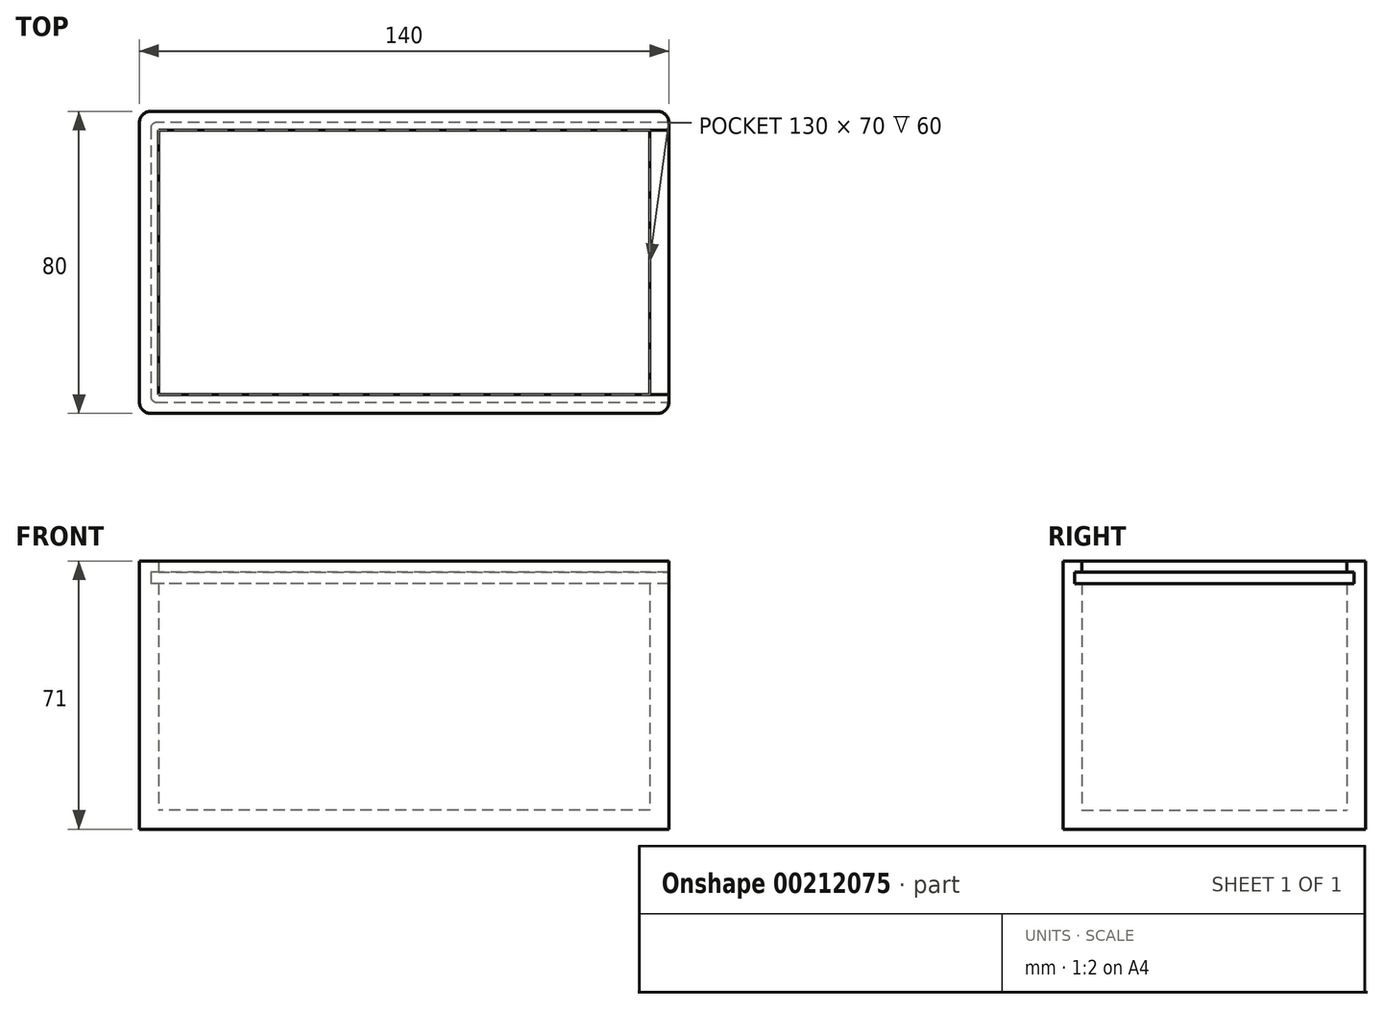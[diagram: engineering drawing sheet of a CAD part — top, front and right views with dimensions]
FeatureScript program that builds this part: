
annotation { "Feature Type Name" : "Feature", "Feature Type Description" : "" }
export const myFeature = defineFeature(function(context is Context, id is Id, definition is map)
    precondition{}
    {
        {
            var Q0;
            Q0=qCreatedBy(makeId("Top.planeOp"),FACE);
            var sketch = newSketch(context, id + "F0", { "sketchPlane" : qUnion([Q0])});
            skLineSegment(sketch, "E0.bottom", {"start": v(70, -40) * mm, "end": v(-70, -40) * mm});
            skLineSegment(sketch, "E0.top", {"start": v(70, 40) * mm, "end": v(-70, 40) * mm});
            skLineSegment(sketch, "E0.left", {"start": v(70, -40) * mm, "end": v(70, 40) * mm});
            skLineSegment(sketch, "E0.right", {"start": v(-70, -40) * mm, "end": v(-70, 40) * mm});
            skPoint(sketch, "E0.middle", {"position": v(0, 0) * mm});
            skLineSegment(sketch, "E1.bottom", {"start": v(65, -35) * mm, "end": v(-65, -35) * mm});
            skLineSegment(sketch, "E1.top", {"start": v(65, 35) * mm, "end": v(-65, 35) * mm});
            skLineSegment(sketch, "E1.left", {"start": v(65, -35) * mm, "end": v(65, 35) * mm});
            skLineSegment(sketch, "E1.right", {"start": v(-65, -35) * mm, "end": v(-65, 35) * mm});
            skSolve(sketch);
        }
        {
            var Q0;
            Q0=makeQuery(id+"F0.imprint","IMPRINT",FACE,{"disambiguationData":[TD([[makeQuery(id+"F0.imprint","IMPRINT",EDGE,{"derivedFrom":sQuery(id+"F0.wireOp",EDGE,"E0.bottom")}),-1.0]])]});
            extrude(context, id + "F1", {"entities" : qUnion([Q0]), "depth" : 70 * mm});
        }
        {
            var Q0;
            Q0=makeQuery(id+"F0.imprint","IMPRINT",FACE,{"disambiguationData":[TD([[makeQuery(id+"F0.imprint","IMPRINT",EDGE,{"derivedFrom":sQuery(id+"F0.wireOp",EDGE,"E1.bottom")}),-1.0]])]});
            extrude(context, id + "F2", {"entities" : qUnion([Q0]), "operationType" : NewBodyOperationType.ADD, "depth" : 5 * mm});
        }
        {
            var Q0;
            Q0=makeQuery(id+"F1.opExtrude","CAP_FACE",FACE,{"disambiguationData":[OSD([sQuery(id+"F0.wireOp",EDGE,"E0.bottom"),sQuery(id+"F0.wireOp",EDGE,"E0.top"),sQuery(id+"F0.wireOp",EDGE,"E0.left"),sQuery(id+"F0.wireOp",EDGE,"E0.right"),sQuery(id+"F0.wireOp",EDGE,"E1.bottom"),sQuery(id+"F0.wireOp",EDGE,"E1.top"),sQuery(id+"F0.wireOp",EDGE,"E1.left"),sQuery(id+"F0.wireOp",EDGE,"E1.right")])],"isStart":false});
            var sketch = newSketch(context, id + "F3", { "sketchPlane" : qUnion([Q0])});
            skLineSegment(sketch, "E2.bottom", {"start": v(65, 35) * mm, "end": v(70, 35) * mm});
            skLineSegment(sketch, "E2.top", {"start": v(65, -35) * mm, "end": v(70, -35) * mm});
            skLineSegment(sketch, "E2.left", {"start": v(65, 35) * mm, "end": v(65, -35) * mm});
            skLineSegment(sketch, "E2.right", {"start": v(70, 35) * mm, "end": v(70, -35) * mm});
            skSolve(sketch);
        }
        {
            var Q0;
            Q0=makeQuery(id+"F3.imprint","IMPRINT",FACE,{"disambiguationData":[TD([[makeQuery(id+"F3.imprint","IMPRINT",EDGE,{"derivedFrom":sQuery(id+"F3.wireOp",EDGE,"E2.bottom")}),-1.0]])]});
            extrude(context, id + "F4", {"entities" : qUnion([Q0]), "operationType" : NewBodyOperationType.REMOVE, "oppositeDirection" : true, "depth" : 5 * mm});
        }
        {
            var Q0;
            Q0=makeQuery(id+"F4.boolean.opBoolean","MERGE",FACE,{"derivedFrom":[makeQuery(id+"F1.opExtrude","SWEPT_FACE",FACE,{"disambiguationData":[OSD([sQuery(id+"F0.wireOp",EDGE,"E1.top")])]}),makeQuery(id+"F4.opExtrude","SWEPT_FACE",FACE,{"disambiguationData":[OSD([sQuery(id+"F3.wireOp",EDGE,"E2.bottom")])]})]});
            var sketch = newSketch(context, id + "F5", { "sketchPlane" : qUnion([Q0])});
            skLineSegment(sketch, "E3.bottom", {"start": v(70, 65) * mm, "end": v(-65, 65) * mm});
            skLineSegment(sketch, "E3.top", {"start": v(70, 68) * mm, "end": v(-65, 68) * mm});
            skLineSegment(sketch, "E3.left", {"start": v(70, 65) * mm, "end": v(70, 68) * mm});
            skLineSegment(sketch, "E3.right", {"start": v(-65, 65) * mm, "end": v(-65, 68) * mm});
            skSolve(sketch);
        }
        {
            var Q0;
            Q0=makeQuery(id+"F5.imprint","IMPRINT",FACE,{"disambiguationData":[TD([[makeQuery(id+"F5.imprint","IMPRINT",EDGE,{"derivedFrom":sQuery(id+"F5.wireOp",EDGE,"E3.bottom")}),-1.0]])]});
            extrude(context, id + "F6", {"entities" : qUnion([Q0]), "operationType" : NewBodyOperationType.REMOVE, "oppositeDirection" : true, "depth" : 2 * mm});
        }
        {
            var Q0;
            Q0=makeQuery(id+"F6.boolean.opBoolean","MERGE",FACE,{"derivedFrom":[makeQuery(id+"F1.opExtrude","SWEPT_FACE",FACE,{"disambiguationData":[OSD([sQuery(id+"F0.wireOp",EDGE,"E1.right")])]}),makeQuery(id+"F6.opExtrude","SWEPT_FACE",FACE,{"disambiguationData":[OSD([sQuery(id+"F5.wireOp",EDGE,"E3.right")])]})]});
            var sketch = newSketch(context, id + "F7", { "sketchPlane" : qUnion([Q0])});
            skLineSegment(sketch, "E4.bottom", {"start": v(37, 65) * mm, "end": v(-35, 65) * mm});
            skLineSegment(sketch, "E4.top", {"start": v(37, 68) * mm, "end": v(-35, 68) * mm});
            skLineSegment(sketch, "E4.left", {"start": v(37, 65) * mm, "end": v(37, 68) * mm});
            skLineSegment(sketch, "E4.right", {"start": v(-35, 65) * mm, "end": v(-35, 68) * mm});
            skSolve(sketch);
        }
        {
            var Q0;
            Q0=makeQuery(id+"F7.imprint","IMPRINT",FACE,{"disambiguationData":[TD([[makeQuery(id+"F7.imprint","IMPRINT",EDGE,{"derivedFrom":sQuery(id+"F7.wireOp",EDGE,"E4.bottom")}),-1.0]])]});
            extrude(context, id + "F8", {"entities" : qUnion([Q0]), "operationType" : NewBodyOperationType.REMOVE, "oppositeDirection" : true, "depth" : 2 * mm});
        }
        {
            var Q0;
            Q0=makeQuery(id+"F8.boolean.opBoolean","MERGE",FACE,{"derivedFrom":[makeQuery(id+"F4.boolean.opBoolean","MERGE",FACE,{"derivedFrom":[makeQuery(id+"F1.opExtrude","SWEPT_FACE",FACE,{"disambiguationData":[OSD([sQuery(id+"F0.wireOp",EDGE,"E1.bottom")])]}),makeQuery(id+"F4.opExtrude","SWEPT_FACE",FACE,{"disambiguationData":[OSD([sQuery(id+"F3.wireOp",EDGE,"E2.top")])]})]}),makeQuery(id+"F8.opExtrude","SWEPT_FACE",FACE,{"disambiguationData":[OSD([sQuery(id+"F7.wireOp",EDGE,"E4.right")])]})]});
            var sketch = newSketch(context, id + "F9", { "sketchPlane" : qUnion([Q0])});
            skLineSegment(sketch, "E5.bottom", {"start": v(67, 65) * mm, "end": v(-70, 65) * mm});
            skLineSegment(sketch, "E5.top", {"start": v(67, 68) * mm, "end": v(-70, 68) * mm});
            skLineSegment(sketch, "E5.left", {"start": v(67, 65) * mm, "end": v(67, 68) * mm});
            skLineSegment(sketch, "E5.right", {"start": v(-70, 65) * mm, "end": v(-70, 68) * mm});
            skSolve(sketch);
        }
        {
            var Q0;
            {var subQ17=sQuery(id+"F9.wireOp",EDGE,"E5.left");Q0=makeQuery(id+"F9.imprint","IMPRINT",FACE,{"disambiguationData":[TD([[makeQuery(id+"F9.imprint","IMPRINT",EDGE,{"derivedFrom":subQ17}),-1.0]])]});}
            extrude(context, id + "F10", {"entities" : qUnion([Q0]), "operationType" : NewBodyOperationType.REMOVE, "oppositeDirection" : true, "depth" : 2 * mm});
        }
        {
            var Q0;
            Q0=makeQuery(id+"F1.opExtrude","SWEPT_EDGE",EDGE,{"disambiguationData":[OSD([sQuery(id+"F0.wireOp",EDGE,"E0.bottom"),sQuery(id+"F0.wireOp",EDGE,"E0.right")])]});
            var Q1;
            Q1=makeQuery(id+"F1.opExtrude","SWEPT_EDGE",EDGE,{"disambiguationData":[OSD([sQuery(id+"F0.wireOp",EDGE,"E0.top"),sQuery(id+"F0.wireOp",EDGE,"E0.right")])]});
            var Q2;
            Q2=makeQuery(id+"F1.opExtrude","SWEPT_EDGE",EDGE,{"disambiguationData":[OSD([sQuery(id+"F0.wireOp",EDGE,"E0.top"),sQuery(id+"F0.wireOp",EDGE,"E0.left")])]});
            var Q3;
            Q3=makeQuery(id+"F1.opExtrude","SWEPT_EDGE",EDGE,{"disambiguationData":[OSD([sQuery(id+"F0.wireOp",EDGE,"E0.bottom"),sQuery(id+"F0.wireOp",EDGE,"E0.left")])]});
            fillet(context, id + "F11", {"entities" : qUnion([Q0, Q1, Q2, Q3]), "radius" : 3 * mm, "tangentPropagation" : true, "allowEdgeOverflow" : false});
        }
        {
            var Q0;
            Q0=makeQuery(id+"F10.boolean.opBoolean","COPY",EDGE,{"derivedFrom":makeQuery(id+"F10.opExtrude","CAP_EDGE",EDGE,{"disambiguationData":[OSD([sQuery(id+"F9.wireOp",EDGE,"E5.left")])],"isStart":false})});
            var Q1;
            Q1=makeQuery(id+"F8.boolean.opBoolean","COPY",EDGE,{"derivedFrom":makeQuery(id+"F8.opExtrude","CAP_EDGE",EDGE,{"disambiguationData":[OSD([sQuery(id+"F7.wireOp",EDGE,"E4.left")])],"isStart":false})});
            fillet(context, id + "F12", {"entities" : qUnion([Q0, Q1]), "radius" : 1.5 * mm, "tangentPropagation" : true, "allowEdgeOverflow" : false});
        }
        {
            var Q0;
            Q0=makeQuery(id+"F1.opExtrude","CAP_FACE",FACE,{"disambiguationData":[OSD([sQuery(id+"F0.wireOp",EDGE,"E0.bottom"),sQuery(id+"F0.wireOp",EDGE,"E0.top"),sQuery(id+"F0.wireOp",EDGE,"E0.left"),sQuery(id+"F0.wireOp",EDGE,"E0.right"),sQuery(id+"F0.wireOp",EDGE,"E1.bottom"),sQuery(id+"F0.wireOp",EDGE,"E1.top"),sQuery(id+"F0.wireOp",EDGE,"E1.left"),sQuery(id+"F0.wireOp",EDGE,"E1.right")])],"isStart":false});
            extrude(context, id + "F13", {"entities" : qUnion([Q0]), "operationType" : NewBodyOperationType.ADD, "depth" : 1 * mm});
        }
    });
